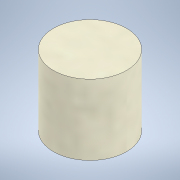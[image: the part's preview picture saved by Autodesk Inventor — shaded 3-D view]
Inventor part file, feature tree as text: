
AUTODESK INVENTOR PART (.ipt)
format: ipt  version: 2021 (Build 250183000, 183)  size: 99,328 bytes
history: native  units: mm
features: extrude x1, sketch x1
ambient origin geometry x8: Origin, YZ Plane, XZ Plane, XY Plane, X Axis, Y Axis, Z Axis, Center Point
bodies: Solid1 (feature_tree)
feature tree (2):
  extrude  "Extrusion1"  Depth=18.3mm TaperAngle=0.0deg
  sketch  "Sketch1"  dims[d0=19.0mm d1=18.3mm d2=0.0mm]
